SOLIDWORKS PART (.sldprt)
format: sldprt  version: not decoded by parser v0  size: 96,768 bytes
history: native  units: mm
features: plane x4, sketch x3, material x1, extrude x1, revolve x1, cut_extrude x1, pattern_circular x1, chamfer x1 (+10 scaffold rows collapsed)
feature tree (23):
  scaffold x10  (default folders/planes/origin — collapsed)
  material  "Matériau <non spécifié>"
  plane  "Plan de face"
  plane  "Plan de dessus"
  plane  "Plan de droite"
  plane  "Plan3"  Offset=6.4mm
  sketch  "Esquisse1"  dims[D1=~2.611009mm]
  extrude  "Extrusion1"  Depth=16mm
  sketch  "Esquisse2"  dims[D1=0.5mm D2=1.2mm]
  revolve  "Révolution1"  Angle=360deg
  sketch  "Esquisse3"
  cut_extrude  "Enlèv. mat.-Extru.1"  Depth=1mm
  pattern_circular  "Répétition circulaire1"  Count=2  [1 undecoded]
  chamfer  "Chanfrein1"  Distance=1.44mm
decode coverage: 7 of 8 modeling features carry decoded parameters
note: ~ marks probable driven/reference dimensions
note: 1 parameter value undecoded
note: suppression state not decoded; provenance and decode notes live in map.json
